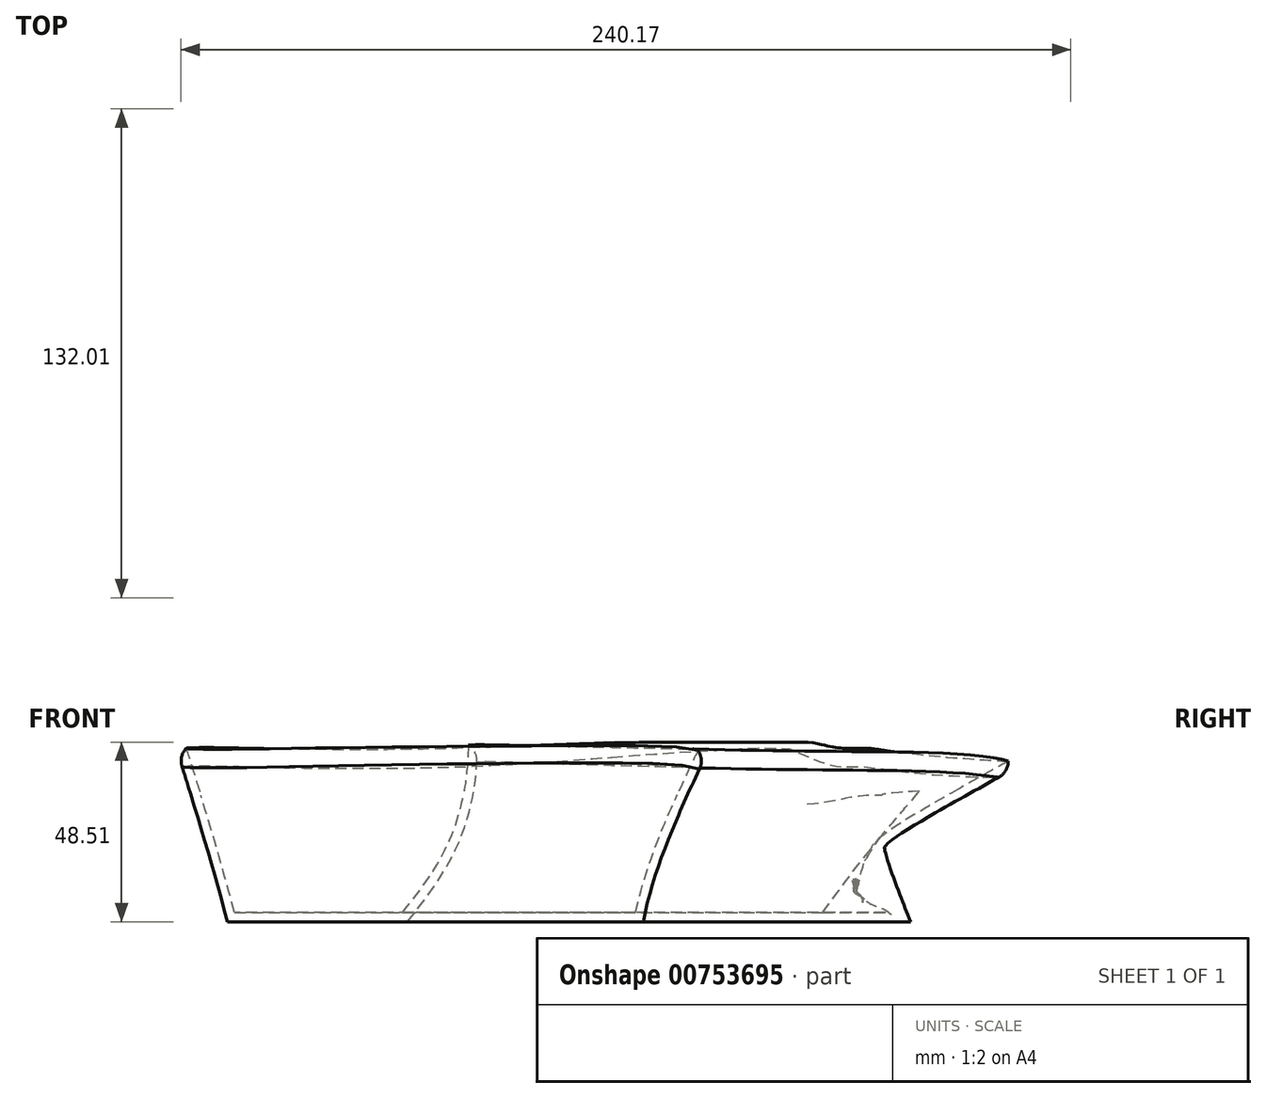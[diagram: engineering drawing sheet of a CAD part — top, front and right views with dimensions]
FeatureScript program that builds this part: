
annotation { "Feature Type Name" : "Feature", "Feature Type Description" : "" }
export const myFeature = defineFeature(function(context is Context, id is Id, definition is map)
    precondition{}
    {
        {
            var Q0;
            Q0=qCreatedBy(makeId("Top.planeOp"),FACE);
            cPlane(context, id + "F0", {"entities" : qUnion([Q0]), "cplaneType" : CPlaneType.OFFSET, "offset" : 48.5 * mm, "width" : 152.4 * mm, "height" : 152.4 * mm});
        }
        {
            var Q0;
            Q0=qCreatedBy(makeId("Top.planeOp"),FACE);
            var sketch = newSketch(context, id + "F1", { "sketchPlane" : qUnion([Q0])});
            skFitSpline(sketch, "E0", {"points": [v(-31.98, 31.98) * mm, v(38.03, 41.75) * mm, v(42.68, 37.56) * mm, v(0, -15.7) * mm, v(-22.9, -18.72) * mm, v(-93.15, -4.54) * mm, v(-31.05, -58.73) * mm, v(-39.89, -74.08) * mm, v(-115.25, -36.63) * mm, v(-137.34, 27.8) * mm, v(-31.98, 31.98) * mm]});
            skSolve(sketch);
        }
        {
            var Q0;
            Q0=qCreatedBy(id+"F0.planeOp",FACE);
            var sketch = newSketch(context, id + "F2", { "sketchPlane" : qUnion([Q0])});
            skFitSpline(sketch, "E1", {"points": [v(34.39, 48.03) * mm, v(10.67, -8.72) * mm, v(-69.8, 47.33) * mm, v(-147.96, 35.47) * mm, v(-123.3, -51.05) * mm, v(-10.73, -70.36) * mm, v(-73.53, -17.33) * mm, v(0, -29.42) * mm, v(83.7, 14.07) * mm, v(34.39, 48.03) * mm]});
            skSolve(sketch);
        }
        {
            var Q0;
            Q0=makeQuery(id+"F1.imprint","IMPRINT",FACE,{"disambiguationData":[TD([[makeQuery(id+"F1.imprint","IMPRINT",EDGE,{"derivedFrom":sQuery(id+"F1.wireOp",EDGE,"E0")}),-1.0]])]});
            var Q1;
            Q1=makeQuery(id+"F2.imprint","IMPRINT",FACE,{"disambiguationData":[TD([[makeQuery(id+"F2.imprint","IMPRINT",EDGE,{"derivedFrom":sQuery(id+"F2.wireOp",EDGE,"E1")}),1.0]])]});
            loft(context, id + "F3", {"sheetProfilesArray" : [{ "sheetProfileEntities" : qUnion([Q0]) }, { "sheetProfileEntities" : qUnion([Q1]) }]});
        }
        {
            var Q0;
            Q0=makeQuery(id+"F3.opLoft","CAP_FACE",FACE,{"disambiguationData":[OSD([makeQuery(id+"F2.imprint","IMPRINT",FACE,{"disambiguationData":[TD([[makeQuery(id+"F2.imprint","IMPRINT",EDGE,{"derivedFrom":sQuery(id+"F2.wireOp",EDGE,"E1")}),1.0]])]})])],"isStart":true});
            shell(context, id + "F4", {"entities" : qUnion([Q0]), "thickness" : 2.54 * mm});
        }
        {
            var Q0;
            Q0=makeQuery(id+"F3.opLoft","MID_CAP_EDGE",EDGE,{"disambiguationData":[OSD([sQuery(id+"F2.wireOp",EDGE,"E1")])],"capPos":1.0});
            fillet(context, id + "F5", {"entities" : qUnion([Q0]), "radius" : 5.08 * mm, "tangentPropagation" : true, "allowEdgeOverflow" : false});
        }
    });
